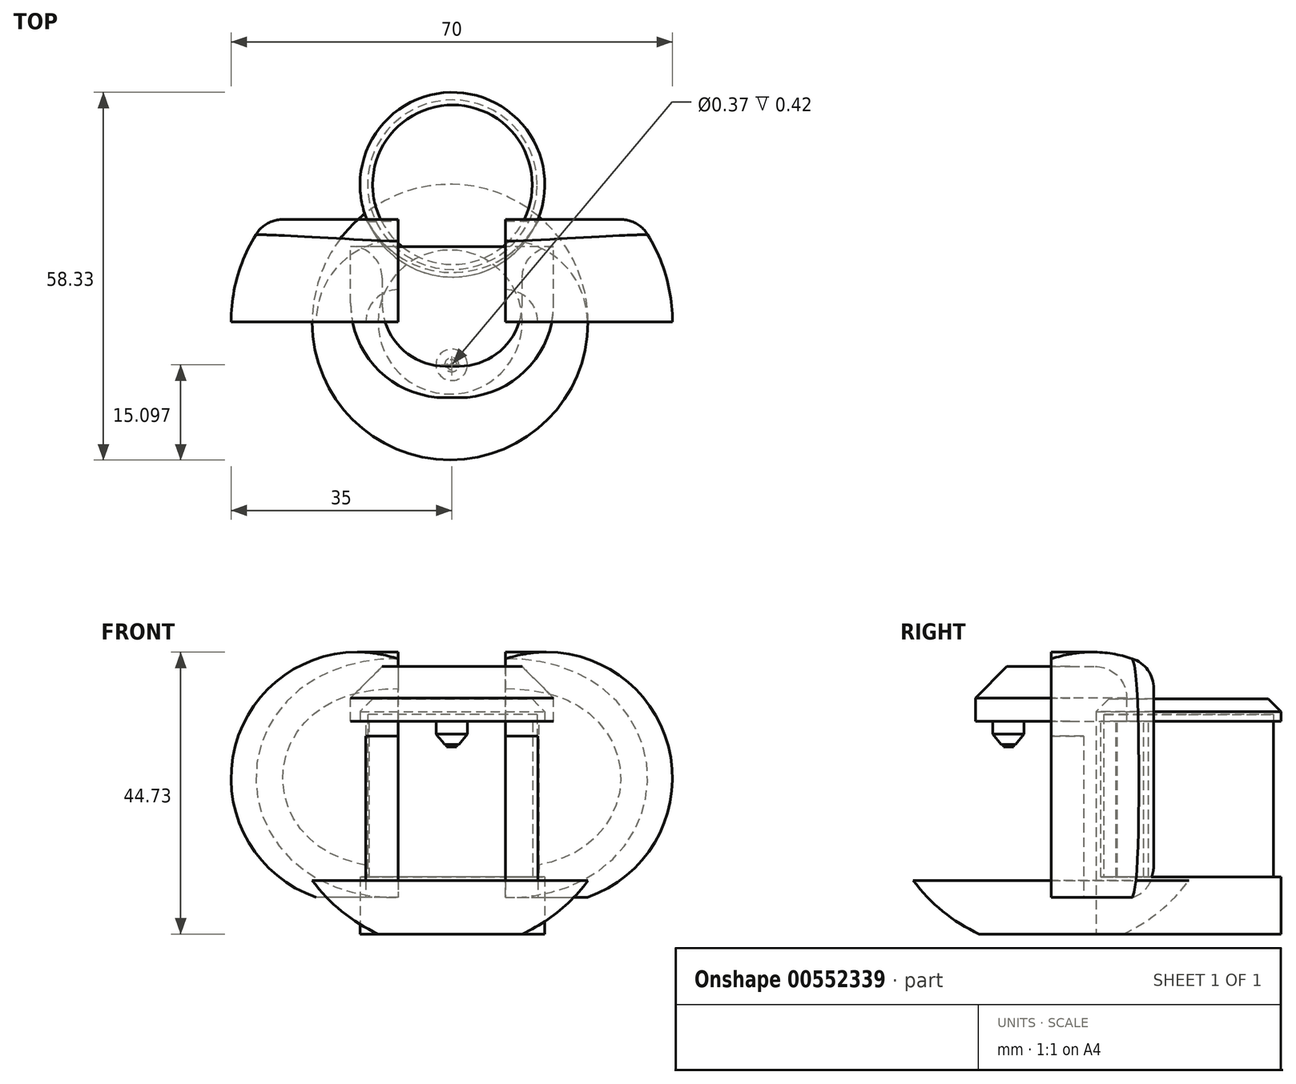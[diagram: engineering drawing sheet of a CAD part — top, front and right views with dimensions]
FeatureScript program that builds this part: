
annotation { "Feature Type Name" : "Feature", "Feature Type Description" : "" }
export const myFeature = defineFeature(function(context is Context, id is Id, definition is map)
    precondition{}
    {
        {
            var Q0;
            Q0=qCreatedBy(makeId("Front.planeOp"),FACE);
            var sketch = newSketch(context, id + "F0", { "sketchPlane" : qUnion([Q0])});
            skArc(sketch, "E0", {"start": v(6.51, 18.9) * mm, "mid": v(-18.9, 6.51) * mm, "end": v(-6.51, -18.9) * mm});
            skLineSegment(sketch, "E1", {"start": v(6.51, 18.9) * mm, "end": v(6.51, 6.67) * mm});
            skLineSegment(sketch, "E2", {"start": v(1.37, -18.9) * mm, "end": v(-6.51, -18.9) * mm});
            skLineSegment(sketch, "E3", {"start": v(6.51, 6.67) * mm, "end": v(1.37, 6.67) * mm});
            skLineSegment(sketch, "E4", {"start": v(1.37, 6.67) * mm, "end": v(1.37, -18.9) * mm});
            skSolve(sketch);
        }
        {
            var Q0;
            Q0 = qSketchRegion(id + "F0", true);
            var Q1;
            Q1=sQuery(id+"F0.wireOp",EDGE,"E1");
            revolve(context, id + "F1", {"entities" : qUnion([Q0]), "axis" : qUnion([Q1]), "revolveType" : RevolveType.ONE_DIRECTION, "angle" : 90 * degree});
        }
        {
            var Q0;
            Q0=qCreatedBy(makeId("Top.planeOp"),FACE);
            var sketch = newSketch(context, id + "F2", { "sketchPlane" : qUnion([Q0])});
            skLineSegment(sketch, "E5", {"start": v(7.4, 16.28) * mm, "end": v(-41.74, 16.28) * mm});
            skLineSegment(sketch, "E6", {"start": v(-41.74, 16.28) * mm, "end": v(-41.74, 43.52) * mm});
            skLineSegment(sketch, "E7", {"start": v(-41.74, 43.52) * mm, "end": v(17.17, 43.52) * mm});
            skLineSegment(sketch, "E8", {"start": v(17.17, 43.52) * mm, "end": v(17.17, 16.28) * mm});
            skLineSegment(sketch, "E9", {"start": v(17.17, 16.28) * mm, "end": v(7.4, 16.28) * mm});
            skSolve(sketch);
        }
        {
            var Q0;
            Q0=makeQuery(id+"F2.imprint","IMPRINT",FACE,{"disambiguationData":[TD([[makeQuery(id+"F2.imprint","IMPRINT",EDGE,{"derivedFrom":sQuery(id+"F2.wireOp",EDGE,"E5")}),-1.0]])]});
            extrude(context, id + "F3", {"entities" : qUnion([Q0]), "operationType" : NewBodyOperationType.REMOVE, "depth" : 64 * mm, "offsetDistance" : 25 * mm, "symmetric" : true});
        }
        {
            var Q0;
            Q0=qCreatedBy(makeId("Right.planeOp"),FACE);
            cPlane(context, id + "F4", {"entities" : qUnion([Q0]), "cplaneType" : CPlaneType.OFFSET, "offset" : 15 * mm, "width" : 150 * mm, "height" : 150 * mm});
        }
        {
            var Q0;
            Q0=makeQuery(id+"F1.opRevolve","SWEPT_BODY",BODY,{"disambiguationData":[OSD([sQuery(id+"F0.wireOp",EDGE,"E0"),sQuery(id+"F0.wireOp",EDGE,"E1"),sQuery(id+"F0.wireOp",EDGE,"E2")])]});
            var Q1;
            Q1=qCreatedBy(id+"F4.planeOp",FACE);
            mirror(context, id + "F5", {"operationType" : NewBodyOperationType.ADD, "entities" : qUnion([Q0]), "mirrorPlane" : qUnion([Q1])});
        }
        {
            var Q0;
            Q0=qCreatedBy(makeId("Front.planeOp"),FACE);
            var sketch = newSketch(context, id + "F6", { "sketchPlane" : qUnion([Q0])});
            skArc(sketch, "E10", {"start": v(-7.13, -16.24) * mm, "mid": v(-2.44, -21.14) * mm, "end": v(3.32, -24.73) * mm});
            skLineSegment(sketch, "E11", {"start": v(-7.13, -16.24) * mm, "end": v(14.74, -16.24) * mm});
            skLineSegment(sketch, "E12", {"start": v(3.32, -24.73) * mm, "end": v(14.74, -24.73) * mm});
            skLineSegment(sketch, "E13", {"start": v(14.74, -16.24) * mm, "end": v(14.74, -24.73) * mm});
            skPoint(sketch, "E13.startSnap0", {"position": v(14.74, -16.24) * mm});
            skPoint(sketch, "E14.trimOffspring.end.orphan", {"position": v(36.61, -16.24) * mm});
            skPoint(sketch, "E15.orphan", {"position": v(14.74, -2.19) * mm});
            skSolve(sketch);
        }
        {
            var Q0;
            Q0=makeQuery(id+"F6.imprint","IMPRINT",FACE,{"disambiguationData":[TD([[makeQuery(id+"F6.imprint","IMPRINT",EDGE,{"derivedFrom":sQuery(id+"F6.wireOp",EDGE,"E10")}),1.0]])]});
            var Q1;
            Q1=sQuery(id+"F6.wireOp",EDGE,"E13");
            revolve(context, id + "F7", {"entities" : qUnion([Q0]), "axis" : qUnion([Q1]), "revolveType" : RevolveType.FULL});
        }
        {
            var Q0;
            Q0=makeQuery(id+"F0.imprint","IMPRINT",FACE,{"disambiguationData":[TD([[makeQuery(id+"F0.imprint","IMPRINT",EDGE,{"derivedFrom":sQuery(id+"F0.wireOp",EDGE,"E0")}),1.0]])]});
            var sketch = newSketch(context, id + "F8", { "sketchPlane" : qUnion([Q0])});
            skLineSegment(sketch, "E16.bottom", {"start": v(31.16, 9.01) * mm, "end": v(-1.03, 9.01) * mm});
            skLineSegment(sketch, "E16.top", {"start": v(31.16, 17.72) * mm, "end": v(-1.03, 17.72) * mm});
            skLineSegment(sketch, "E16.left", {"start": v(31.16, 9.01) * mm, "end": v(31.16, 17.72) * mm});
            skLineSegment(sketch, "E16.right", {"start": v(-1.03, 9.01) * mm, "end": v(-1.03, 17.72) * mm});
            skPoint(sketch, "E16.middle", {"position": v(15.06, 13.37) * mm});
            skSolve(sketch);
        }
        {
            var Q0;
            Q0 = qSketchRegion(id + "F8", true);
            extrude(context, id + "F9", {"entities" : qUnion([Q0]), "depth" : 24 * mm, "offsetDistance" : 25 * mm, "symmetric" : true});
        }
        {
            var Q0;
            Q0=makeQuery(id+"F9.opExtrude","CAP_EDGE",EDGE,{"disambiguationData":[OSD([sQuery(id+"F8.wireOp",EDGE,"E16.left")])],"isStart":false});
            var Q1;
            Q1=makeQuery(id+"F9.opExtrude","CAP_EDGE",EDGE,{"disambiguationData":[OSD([sQuery(id+"F8.wireOp",EDGE,"E16.right")])],"isStart":false});
            fillet(context, id + "F10", {"entities" : qUnion([Q0, Q1]), "radius" : 15 * mm, "tangentPropagation" : true, "allowEdgeOverflow" : false});
        }
        {
            var Q0;
            Q0=makeQuery(id+"F7.opRevolve","SWEPT_FACE",FACE,{"disambiguationData":[OSD([sQuery(id+"F6.wireOp",EDGE,"E12")])]});
            var sketch = newSketch(context, id + "F11", { "sketchPlane" : qUnion([Q0])});
            skCircle(sketch, "E17", {"center": v(15.1, -21.8) * mm, "radius": 14.65 * mm});
            skSolve(sketch);
        }
        {
            var Q0;
            {var subQ0=sQuery(id+"F11.wireOp",EDGE,"E17");var subQ1=makeQuery(id+"F7.opRevolve","SWEPT_EDGE",EDGE,{"disambiguationData":[OSD([sQuery(id+"F6.wireOp",EDGE,"E10"),sQuery(id+"F6.wireOp",EDGE,"E12")])]});var subQ2=makeQuery(id+"F11.imprint","INTERSECT",VERTEX,{"disambiguationData":[OD(0.0)],"derivedFrom":[subQ1,subQ0]});Q0=makeQuery(id+"F11.imprint","IMPRINT",FACE,{"disambiguationData":[TD([[makeQuery(id+"F11.imprint","IMPRINT",EDGE,{"disambiguationData":[TD([[subQ2,-1.0]])],"derivedFrom":subQ0}),1.0]])]});}
            var Q1;
            {var subQ0=sQuery(id+"F11.wireOp",EDGE,"E17");var subQ1=makeQuery(id+"F7.opRevolve","SWEPT_EDGE",EDGE,{"disambiguationData":[OSD([sQuery(id+"F6.wireOp",EDGE,"E10"),sQuery(id+"F6.wireOp",EDGE,"E12")])]});var subQ2=makeQuery(id+"F11.imprint","INTERSECT",VERTEX,{"disambiguationData":[OD(0.0)],"derivedFrom":[subQ1,subQ0]});Q1=makeQuery(id+"F11.imprint","IMPRINT",FACE,{"disambiguationData":[TD([[makeQuery(id+"F11.imprint","IMPRINT",EDGE,{"disambiguationData":[TD([[subQ2,1.0]])],"derivedFrom":subQ0}),1.0]])]});}
            extrude(context, id + "F12", {"entities" : qUnion([Q0, Q1]), "oppositeDirection" : true, "depth" : 37.3 * mm, "offsetDistance" : 25 * mm});
        }
        {
            var Q0;
            Q0=makeQuery(id+"F5.opPattern","COPY",EDGE,{"derivedFrom":makeQuery(id+"F3.boolean.opBoolean","INTERSECT",EDGE,{"derivedFrom":[makeQuery(id+"F1.opRevolve","SWEPT_FACE",FACE,{"disambiguationData":[OSD([sQuery(id+"F0.wireOp",EDGE,"E0")])]}),makeQuery(id+"F3.opExtrude","SWEPT_FACE",FACE,{"disambiguationData":[OSD([sQuery(id+"F2.wireOp",EDGE,"E5"),sQuery(id+"F2.wireOp",EDGE,"E9")])]})]}),"instanceName":"1"});
            var Q1;
            Q1=makeQuery(id+"F3.boolean.opBoolean","INTERSECT",EDGE,{"derivedFrom":[makeQuery(id+"F1.opRevolve","SWEPT_FACE",FACE,{"disambiguationData":[OSD([sQuery(id+"F0.wireOp",EDGE,"E0")])]}),makeQuery(id+"F3.opExtrude","SWEPT_FACE",FACE,{"disambiguationData":[OSD([sQuery(id+"F2.wireOp",EDGE,"E5"),sQuery(id+"F2.wireOp",EDGE,"E9")])]})]});
            fillet(context, id + "F13", {"entities" : qUnion([Q0, Q1]), "radius" : 5 * mm, "tangentPropagation" : true, "allowEdgeOverflow" : false});
        }
        {
            var Q0;
            Q0=makeQuery(id+"F12.opExtrude","CAP_EDGE",EDGE,{"disambiguationData":[OSD([sQuery(id+"F11.wireOp",EDGE,"E17")])],"isStart":false});
            chamfer(context, id + "F14", {"entities" : qUnion([Q0]), "width" : 2 * mm, "tangentPropagation" : true});
        }
        {
            var Q0;
            Q0=makeQuery(id+"F10.opFillet","BLEND_EDGE",EDGE,{"blendedFrom":[makeQuery(id+"F9.opExtrude","CAP_EDGE",EDGE,{"disambiguationData":[OSD([sQuery(id+"F8.wireOp",EDGE,"E16.left")])],"isStart":false}),makeQuery(id+"F9.opExtrude","SWEPT_FACE",FACE,{"disambiguationData":[OSD([sQuery(id+"F8.wireOp",EDGE,"E16.top")])]})],"blendedInto":[makeQuery(id+"F9.opExtrude","SWEPT_FACE",FACE,{"disambiguationData":[OSD([sQuery(id+"F8.wireOp",EDGE,"E16.top")])]})]});
            chamfer(context, id + "F15", {"entities" : qUnion([Q0]), "width" : 5 * mm, "tangentPropagation" : true});
        }
        {
            var Q0;
            Q0=qCreatedBy(makeId("Top.planeOp"),FACE);
            var sketch = newSketch(context, id + "F16", { "sketchPlane" : qUnion([Q0])});
            skCircle(sketch, "E18", {"center": v(15.15, 23.22) * mm, "radius": 15.35 * mm});
            skSolve(sketch);
        }
        {
            var Q0;
            Q0 = qSketchRegion(id + "F16", true);
            extrude(context, id + "F17", {"entities" : qUnion([Q0]), "operationType" : NewBodyOperationType.REMOVE, "oppositeDirection" : true, "depth" : 15.7 * mm, "offsetDistance" : 25 * mm, "hasSecondDirection" : true, "secondDirectionOppositeDirection" : false, "secondDirectionDepth" : 9 * mm});
        }
        {
            var Q0;
            Q0=makeQuery(id+"F17.boolean.opBoolean","COPY",FACE,{"derivedFrom":makeQuery(id+"F17.opExtrude","CAP_FACE",FACE,{"disambiguationData":[OSD([sQuery(id+"F16.wireOp",EDGE,"E18")])],"isStart":false})});
            var sketch = newSketch(context, id + "F18", { "sketchPlane" : qUnion([Q0])});
            skCircle(sketch, "E19", {"center": v(15.1, 21.8) * mm, "radius": 13.45 * mm});
            skSolve(sketch);
        }
        {
            var Q0;
            Q0 = qSketchRegion(id + "F18", true);
            extrude(context, id + "F19", {"entities" : qUnion([Q0]), "depth" : 25.8 * mm, "offsetDistance" : 25 * mm});
        }
        {
            var Q0;
            Q0=makeQuery(id+"F9.opExtrude","CAP_EDGE",EDGE,{"disambiguationData":[OSD([sQuery(id+"F8.wireOp",EDGE,"E16.top")])],"isStart":true});
            fillet(context, id + "F20", {"entities" : qUnion([Q0]), "radius" : 5 * mm, "tangentPropagation" : true, "allowEdgeOverflow" : false});
        }
        {
            var Q0;
            Q0=qCreatedBy(id+"F4.planeOp",FACE);
            var sketch = newSketch(context, id + "F21", { "sketchPlane" : qUnion([Q0])});
            skLineSegment(sketch, "E20", {"start": v(-9.27, 8.98) * mm, "end": v(-9.27, 7) * mm});
            skLineSegment(sketch, "E21", {"start": v(-9.27, 7) * mm, "end": v(-7.9, 5.36) * mm});
            skLineSegment(sketch, "E22", {"start": v(-7.9, 5.36) * mm, "end": v(-7.57, 5.36) * mm});
            skLineSegment(sketch, "E23", {"start": v(-7.57, 5.36) * mm, "end": v(-7.57, 4.94) * mm});
            skLineSegment(sketch, "E24", {"start": v(-7.57, 4.94) * mm, "end": v(-6.96, 4.94) * mm});
            skLineSegment(sketch, "E25", {"start": v(-6.96, 4.94) * mm, "end": v(-6.96, 5.36) * mm});
            skLineSegment(sketch, "E26", {"start": v(-6.96, 5.36) * mm, "end": v(-6.77, 5.36) * mm});
            skLineSegment(sketch, "E27", {"start": v(-6.77, 5.36) * mm, "end": v(-6.77, 9.02) * mm});
            skLineSegment(sketch, "E28", {"start": v(-6.77, 9.02) * mm, "end": v(-9.27, 9.02) * mm});
            skLineSegment(sketch, "E29", {"start": v(-9.27, 9.02) * mm, "end": v(-9.27, 8.98) * mm});
            skSolve(sketch);
        }
        {
            var Q0;
            Q0=makeQuery(id+"F21.imprint","IMPRINT",FACE,{"disambiguationData":[TD([[makeQuery(id+"F21.imprint","IMPRINT",EDGE,{"derivedFrom":sQuery(id+"F21.wireOp",EDGE,"E20")}),1.0]])]});
            var Q1;
            Q1=sQuery(id+"F21.wireOp",EDGE,"E27");
            revolve(context, id + "F22", {"operationType" : NewBodyOperationType.ADD, "entities" : qUnion([Q0]), "axis" : qUnion([Q1]), "revolveType" : RevolveType.FULL});
        }
    });
